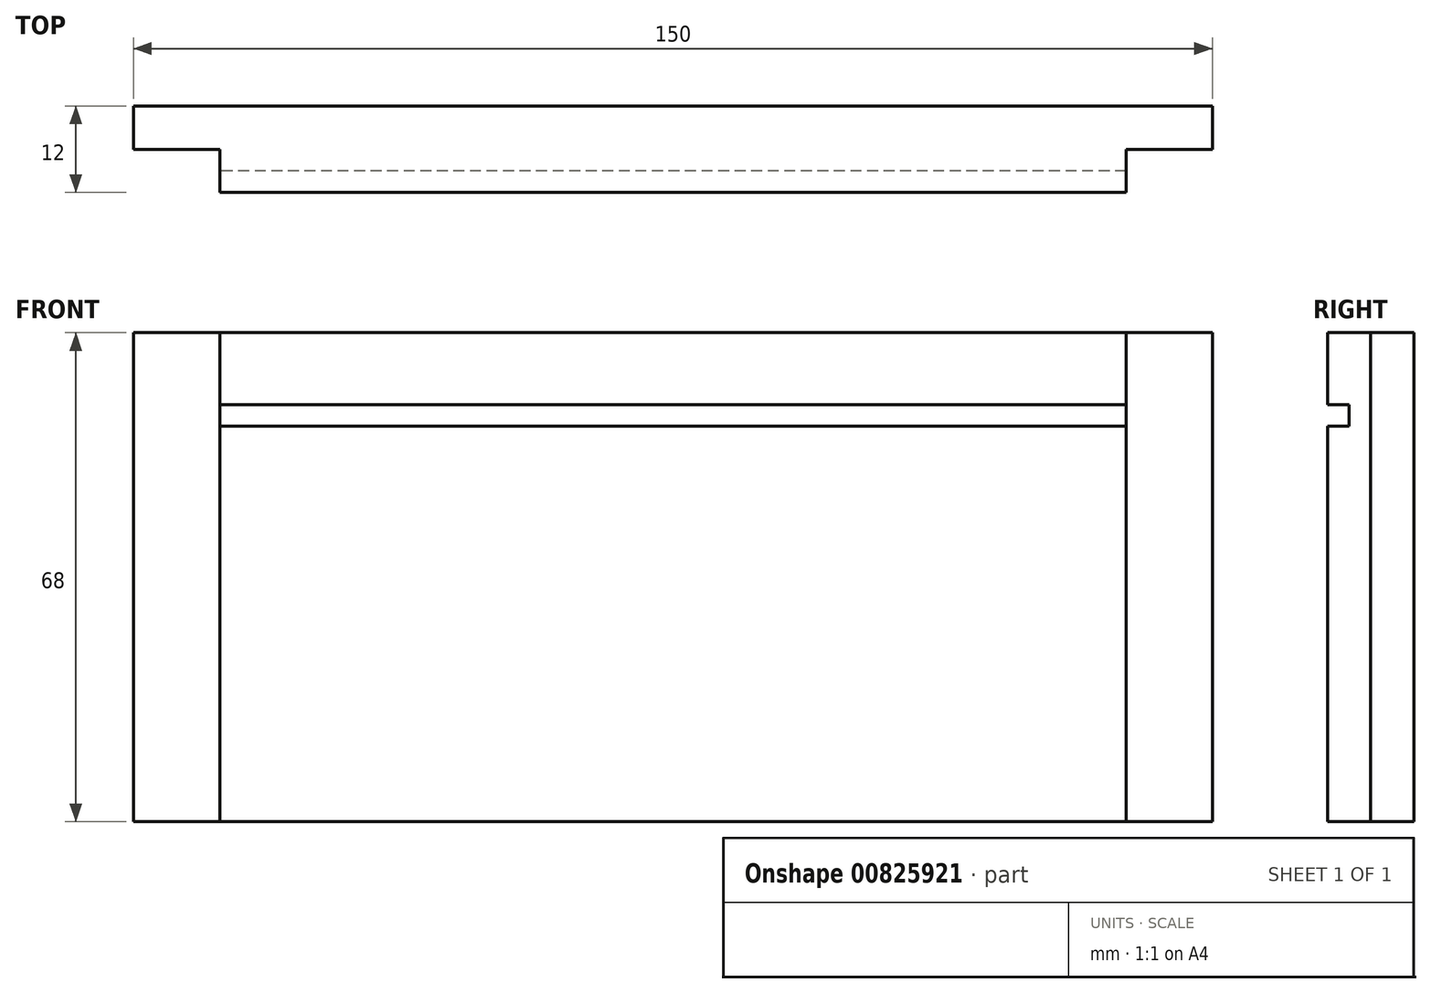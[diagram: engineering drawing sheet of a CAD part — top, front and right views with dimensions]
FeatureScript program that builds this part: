
annotation { "Feature Type Name" : "Feature", "Feature Type Description" : "" }
export const myFeature = defineFeature(function(context is Context, id is Id, definition is map)
    precondition{}
    {
        {
            var Q0;
            Q0=qCreatedBy(makeId("Right.planeOp"),FACE);
            var sketch = newSketch(context, id + "F0", { "sketchPlane" : qUnion([Q0])});
            skLineSegment(sketch, "E0.bottom", {"start": v(0, 0) * mm, "end": v(12, 0) * mm});
            skLineSegment(sketch, "E0.top", {"start": v(0, 68) * mm, "end": v(12, 68) * mm});
            skLineSegment(sketch, "E0.left", {"start": v(0, 0) * mm, "end": v(0, 55) * mm});
            skLineSegment(sketch, "E0.right", {"start": v(12, 0) * mm, "end": v(12, 68) * mm});
            skLineSegment(sketch, "E1.bottom", {"start": v(0, 58) * mm, "end": v(3, 58) * mm});
            skLineSegment(sketch, "E1.top", {"start": v(0, 55) * mm, "end": v(3, 55) * mm});
            skLineSegment(sketch, "E1.right", {"start": v(3, 58) * mm, "end": v(3, 55) * mm});
            skLineSegment(sketch, "E2.trimOffspring", {"start": v(0, 58) * mm, "end": v(0, 68) * mm});
            skSolve(sketch);
        }
        {
            var Q0;
            Q0 = qSketchRegion(id + "F0", true);
            extrude(context, id + "F1", {"entities" : qUnion([Q0]), "depth" : 150 * mm, "offsetDistance" : 25 * mm});
        }
        {
            var Q0;
            Q0=makeQuery(id+"F1.opExtrude","SWEPT_FACE",FACE,{"disambiguationData":[OSD([sQuery(id+"F0.wireOp",EDGE,"E0.top")])]});
            var sketch = newSketch(context, id + "F2", { "sketchPlane" : qUnion([Q0])});
            skLineSegment(sketch, "E3", {"start": v(0, 6) * mm, "end": v(12, 6) * mm});
            skLineSegment(sketch, "E4", {"start": v(12, 6) * mm, "end": v(12, 0) * mm});
            skLineSegment(sketch, "E5", {"start": v(150, 6) * mm, "end": v(138, 6) * mm});
            skLineSegment(sketch, "E6", {"start": v(138, 6) * mm, "end": v(138, 0) * mm});
            skSolve(sketch);
        }
        {
            var Q0;
            Q0 = qSketchRegion(id + "F2", true);
            var Q1;
            {var subQ0=sQuery(id+"F2.wireOp",EDGE,"E3");Q1=makeQuery(id+"F2.imprint","IMPRINT",FACE,{"disambiguationData":[TD([[makeQuery(id+"F2.imprint","IMPRINT",EDGE,{"derivedFrom":subQ0}),-1.0]])]});}
            var Q2;
            {var subQ0=sQuery(id+"F2.wireOp",EDGE,"E5");Q2=makeQuery(id+"F2.imprint","IMPRINT",FACE,{"disambiguationData":[TD([[makeQuery(id+"F2.imprint","IMPRINT",EDGE,{"derivedFrom":subQ0}),1.0]])]});}
            extrude(context, id + "F3", {"entities" : qUnion([Q0, Q1, Q2]), "operationType" : NewBodyOperationType.REMOVE, "oppositeDirection" : true, "depth" : 108.3 * mm, "offsetDistance" : 25 * mm});
        }
    });
